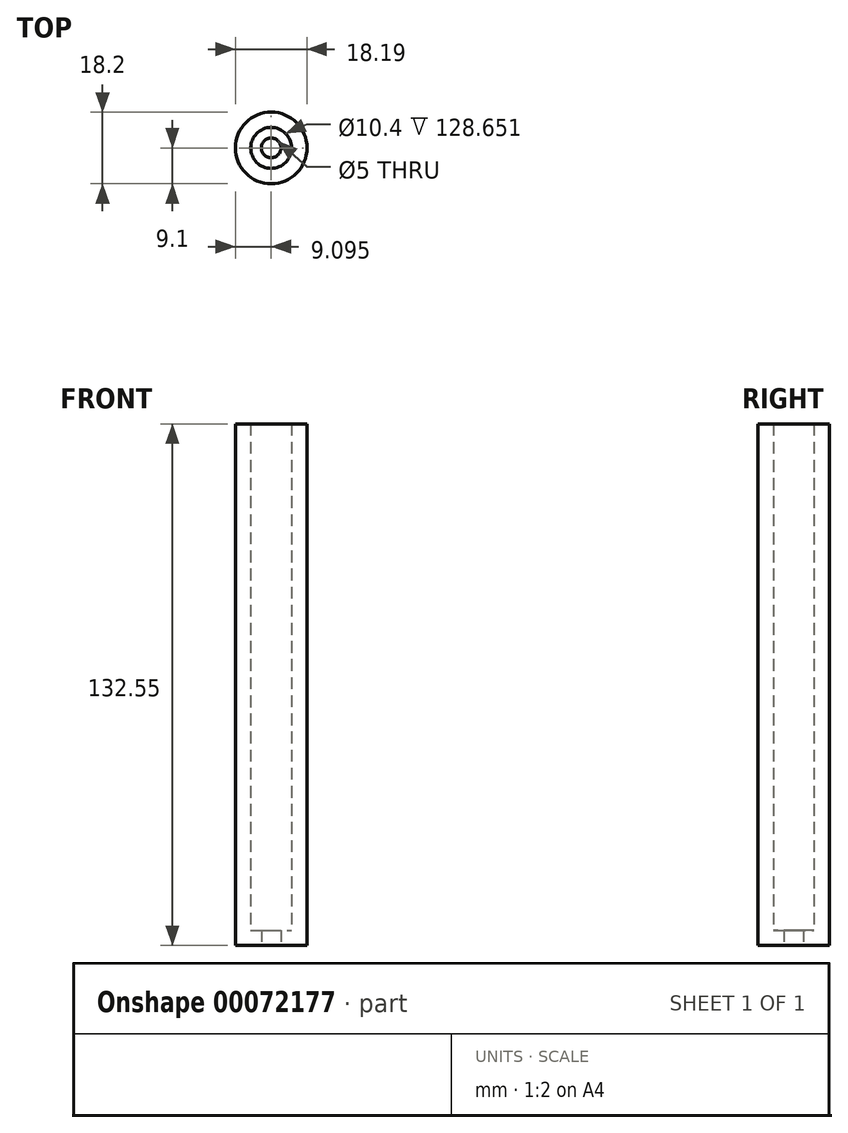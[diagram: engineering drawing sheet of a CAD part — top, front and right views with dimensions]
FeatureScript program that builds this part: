
annotation { "Feature Type Name" : "Feature", "Feature Type Description" : "" }
export const myFeature = defineFeature(function(context is Context, id is Id, definition is map)
    precondition{}
    {
        {
            var Q0;
            Q0=qCreatedBy(makeId("Front.planeOp"),FACE);
            var sketch = newSketch(context, id + "F0", { "sketchPlane" : qUnion([Q0])});
            skLineSegment(sketch, "E0", {"start": v(-48.08, 57.18) * mm, "end": v(-48.08, -75.37) * mm});
            skLineSegment(sketch, "E1", {"start": v(-48.08, -75.37) * mm, "end": v(-38.99, -75.37) * mm});
            skLineSegment(sketch, "E2", {"start": v(-38.99, -75.37) * mm, "end": v(-38.99, -71.47) * mm});
            skLineSegment(sketch, "E3", {"start": v(-38.99, -71.47) * mm, "end": v(-44.18, -71.47) * mm});
            skLineSegment(sketch, "E4", {"start": v(-44.18, -71.47) * mm, "end": v(-44.18, 57.18) * mm});
            skLineSegment(sketch, "E5", {"start": v(-44.18, 57.18) * mm, "end": v(-48.08, 57.18) * mm});
            skSolve(sketch);
        }
        {
            var Q0;
            Q0=makeQuery(id+"F0.imprint","IMPRINT",FACE,{"disambiguationData":[TD([[makeQuery(id+"F0.imprint","IMPRINT",EDGE,{"derivedFrom":sQuery(id+"F0.wireOp",EDGE,"E0")}),1.0]])]});
            var Q1;
            Q1=sQuery(id+"F0.wireOp",EDGE,"E2");
            revolve(context, id + "F1", {"entities" : qUnion([Q0]), "axis" : qUnion([Q1]), "revolveType" : RevolveType.FULL});
        }
        {
            var Q0;
            Q0=makeQuery(id+"F1.opRevolve","SWEPT_FACE",FACE,{"disambiguationData":[OSD([sQuery(id+"F0.wireOp",EDGE,"E1")])]});
            var sketch = newSketch(context, id + "F2", { "sketchPlane" : qUnion([Q0])});
            skCircle(sketch, "E6", {"center": v(-38.99, 0) * mm, "radius": 6.58 * mm});
            skSolve(sketch);
        }
        {
            var Q0;
            Q0=sQuery(id+"F2.wireOp",VERTEX,"E6.center");
            var Q1;
            Q1=makeQuery(id+"F1.opRevolve","SWEPT_BODY",BODY,{"disambiguationData":[OSD([sQuery(id+"F0.wireOp",EDGE,"E0"),sQuery(id+"F0.wireOp",EDGE,"E1"),sQuery(id+"F0.wireOp",EDGE,"E2"),sQuery(id+"F0.wireOp",EDGE,"E3"),sQuery(id+"F0.wireOp",EDGE,"E4"),sQuery(id+"F0.wireOp",EDGE,"E5")])]});
            hole(context, id + "F3", {"style" : HoleStyle.SIMPLE, "holeDiameter" : 5 * mm, "endStyle" : HoleEndStyle.THROUGH, "locations" : qUnion([Q0]), "scope" : qUnion([Q1])});
        }
    });
